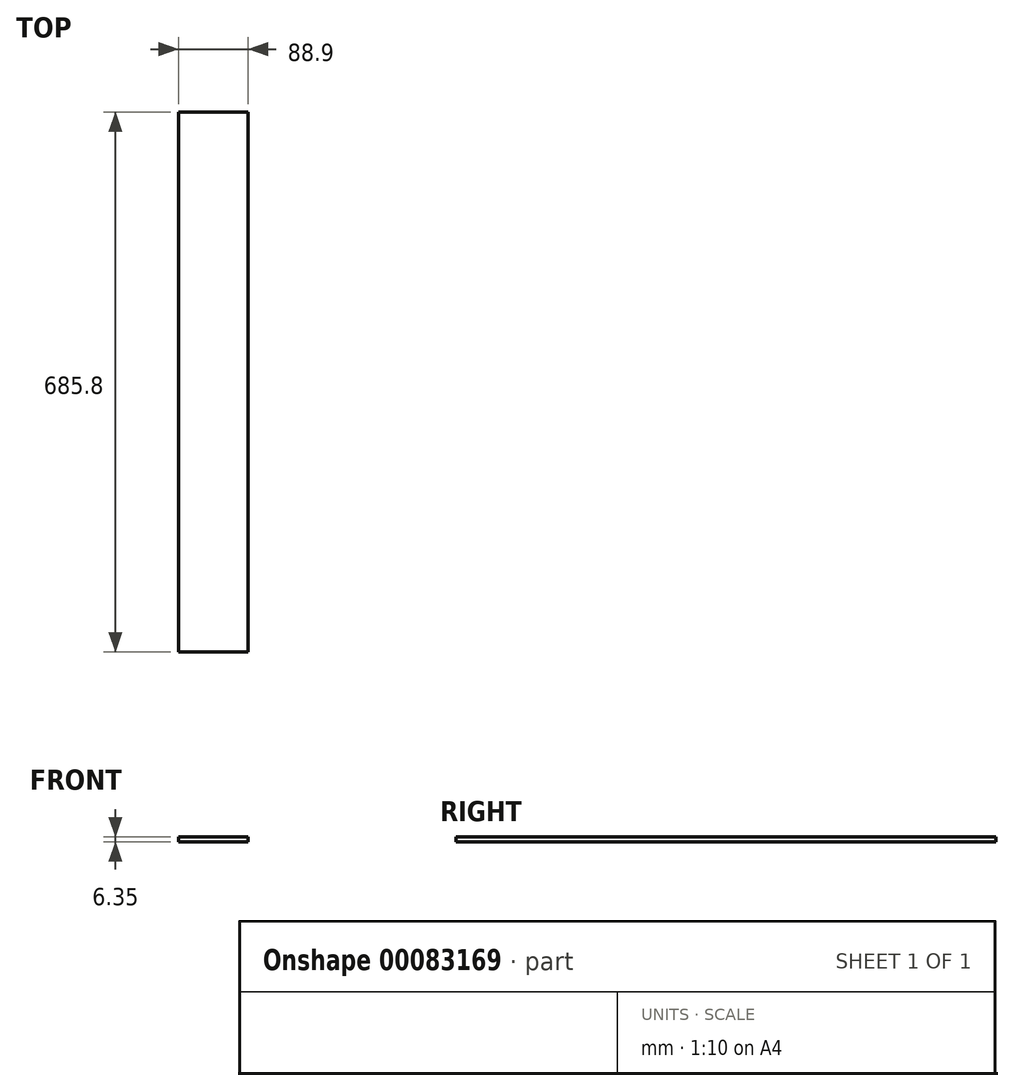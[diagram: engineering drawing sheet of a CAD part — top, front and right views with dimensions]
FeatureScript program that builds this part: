
annotation { "Feature Type Name" : "Feature", "Feature Type Description" : "" }
export const myFeature = defineFeature(function(context is Context, id is Id, definition is map)
    precondition{}
    {
        {
            var Q0;
            Q0=qCreatedBy(makeId("Top.planeOp"),FACE);
            var sketch = newSketch(context, id + "F0", { "sketchPlane" : qUnion([Q0])});
            skLineSegment(sketch, "E0.bottom", {"start": v(44.45, 342.9) * mm, "end": v(-44.45, 342.9) * mm});
            skLineSegment(sketch, "E0.top", {"start": v(44.45, -342.9) * mm, "end": v(-44.45, -342.9) * mm});
            skLineSegment(sketch, "E0.left", {"start": v(44.45, 342.9) * mm, "end": v(44.45, -342.9) * mm});
            skLineSegment(sketch, "E0.right", {"start": v(-44.45, 342.9) * mm, "end": v(-44.45, -342.9) * mm});
            skPoint(sketch, "E0.middle", {"position": v(0, 0) * mm});
            skSolve(sketch);
        }
        {
            var Q0;
            Q0=makeQuery(id+"F0.imprint","IMPRINT",FACE,{"disambiguationData":[TD([[makeQuery(id+"F0.imprint","IMPRINT",EDGE,{"derivedFrom":sQuery(id+"F0.wireOp",EDGE,"E0.bottom")}),1.0]])]});
            extrude(context, id + "F1", {"entities" : qUnion([Q0]), "depth" : 6.35 * mm});
        }
    });
